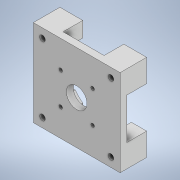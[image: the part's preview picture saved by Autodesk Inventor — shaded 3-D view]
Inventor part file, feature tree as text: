
AUTODESK INVENTOR PART (.ipt)
format: ipt  version: 2022.2 (Build 262287030, 287C)  size: 185,344 bytes
history: native  units: in
note: dims shown in document units (in); Inventor stores cm internally (conversion verified against a paired STEP export)
features: sketch x7, extrude x4, hole x3, projected_geometry x1
ambient origin geometry x8: Origin, YZ Plane, XZ Plane, XY Plane, X Axis, Y Axis, Z Axis, Center Point
bodies: Solid1 (feature_tree)
feature tree (15):
  extrude  "Extrusion1"  Depth=1.4961in
  sketch  "Sketch4"  dims[d2=0.3543in d3=0.4583in d4=0.0in]
  extrude  "Extrusion2"  Depth=0.4583in TaperAngle=0.0deg
  extrude  "Extrusion3"  Depth=0.8858in
  extrude  "Extrusion4"  Depth=0.3402in TaperAngle=0.0deg
  hole  "Hole1"  [1 undecoded]
  hole  "Hole2"  [1 undecoded]
  hole  "Hole3"  [1 undecoded]
  sketch  "Sketch1"  dims[d0=1.4961in d1=1.4961in]
  sketch  "Sketch5"  dims[d17=0.8858in d18=0.8858in]
  sketch  "Sketch6"  dims[d19=1.2in d20=0.3402in d21=0.0in]
  sketch  "Sketch7"  dims[d22=0.3937in d23=0.3937in]
  sketch  "Sketch8"  dims[d24=0.0in d25=0.0in d26=0.3937in]
  projected_geometry  "Projected Loop1"
  sketch  "Sketch9"  dims[d27=0.3937in d28=0.0in d29=0.0in d30=0.5906in d31=0.5906in d32=0.7874in d34=1.1811in d35=0.7874in d37=1.1811in d40=0.0984in d41=0.1575in d42=0.1476in d43=0.0984in d44=90.0deg d45=0.1575in d46=0.0in d47=0.2756in d48=0.2756in d49=0.7874in d51=0.5512in d52=0.7874in d54=0.5512in d57=0.0617in d58=0.1575in d59=0.1476in d60=0.0984in d61=90.0deg d62=0.3937in d63=0.0in d64=0.0984in d65=0.1181in d66=0.1476in d67=0.0984in d68=90.0deg d69=0.1181in d70=0.0in d12=0.0in d13=0.0in d14=0.0in d15=0.0in d16=0.0in d71=0.2953in d72=0.8108in d73=0.0246in d74=0.2953in d75=0.1476in]
note: 3 required parameter values undecoded (feature->parameter linkage not recoverable at this tier; creation-order binding heuristic only, values carry confidence <= 0.55)
